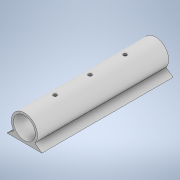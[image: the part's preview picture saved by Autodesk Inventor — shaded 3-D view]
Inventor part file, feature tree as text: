
AUTODESK INVENTOR PART (.ipt)
format: ipt  version: 2022 (Build 260153000, 153)  size: 148,480 bytes
history: native  units: in
note: dims shown in document units (in); Inventor stores cm internally (conversion verified against a paired STEP export)
features: extrude x3, sketch x3
ambient origin geometry x8: Origin, YZ Plane, XZ Plane, XY Plane, X Axis, Y Axis, Z Axis, Center Point
bodies: Solid1 (feature_tree)
feature tree (6):
  extrude  "Extrusion1"  Depth=5.9055in
  extrude  "Extrusion2"  Depth=1.1811in TaperAngle=0.0deg
  extrude  "Extrusion3"  Depth=0.9843in
  sketch  "Sketch1"  dims[d0=2.3622in d1=5.9055in]
  sketch  "Sketch2"  dims[d2=1.5748in d3=1.1811in d4=0.0in]
  sketch  "Sketch3"  dims[d5=1.5748in d6=1.5748in d7=0.1299in d8=0.1378in d9=0.1378in d10=0.1378in d11=0.1575in d12=0.1575in d13=0.1575in d14=0.1575in d15=0.0in d16=1.1811in d17=0.1969in d18=0.9843in d19=5.9055in d20=0.0in]
